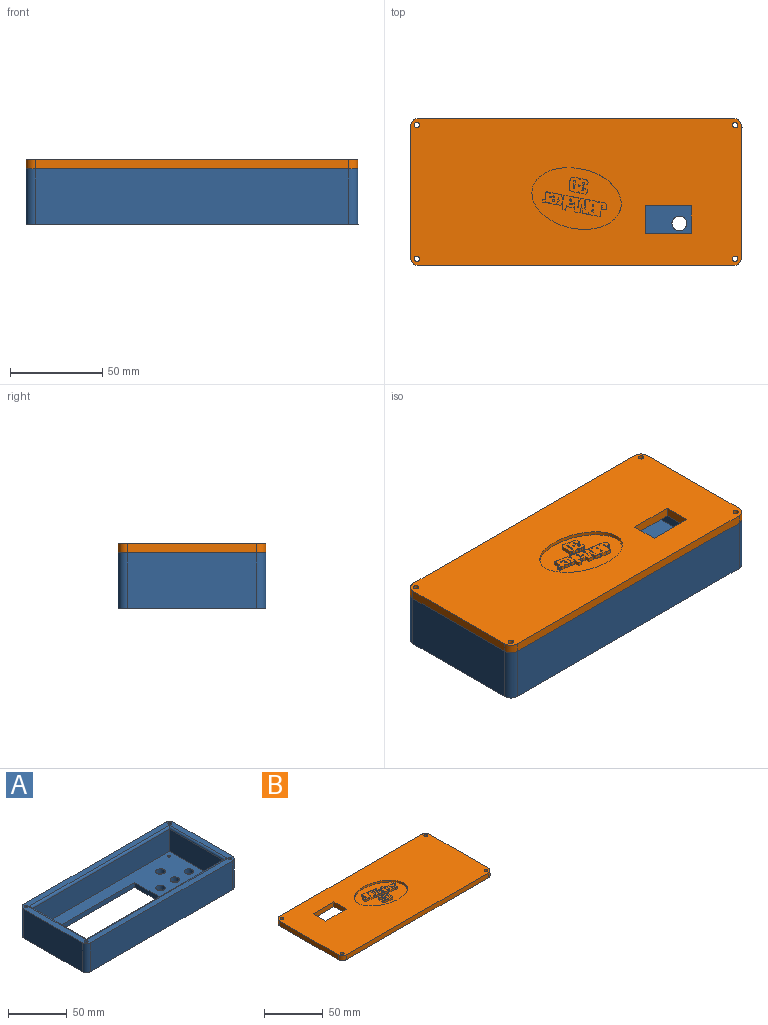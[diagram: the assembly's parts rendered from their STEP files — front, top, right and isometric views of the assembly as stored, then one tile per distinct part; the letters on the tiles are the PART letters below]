
ASSEMBLY  parts=2 mates=1
PART A: 36 faces, bbox 180x80x30 mm
  f0: plane 165x65mm, normal (0,0,1), area 6145.4mm2, adj f2,f3,f4,f9,f11,f12,f13,f14
  f1: plane 180x80mm, normal (0,0,-1), area 9770.7mm2, adj f5,f6,f7,f8,f11,f12,f13,f14
  f2: plane 165x23mm, normal (0,1,0), area 3795mm2, adj f0,f3,f9,f32
  f3: plane 65x23mm, normal (1,0,0), area 1495mm2, adj f0,f2,f4,f33
  f4: plane 165x23mm, normal (0,-1,0), area 3795mm2, adj f0,f3,f9,f35
  f5: plane 70x30mm, normal (-1,0,0), area 2100mm2, adj f1,f10,f28,f31
  f6: plane 170x30mm, normal (0,-1,0), area 5100mm2, adj f1,f10,f28,f29
  f7: plane 70x30mm, normal (1,0,0), area 2100mm2, adj f1,f10,f29,f30
  f8: plane 170x30mm, normal (0,1,0), area 5100mm2, adj f1,f10,f30,f31
  f9: plane 65x23mm, normal (-1,0,0), area 1495mm2, adj f0,f2,f4,f34
  f10: plane 180x80mm, normal (0,0,1), area 2689.3mm2, adj f5,f6,f7,f8,f24,f25,f26,f27
  f11: cylinder r=1.5mm len=5mm, axis (0,0,1), area 47.1mm2, adj f0,f1
  f12: cylinder r=4mm len=8mm, axis (0,0,1), area 125.7mm2, adj f0,f1
  f13: plane 100x5mm, normal (0,-1,0), area 500mm2, adj f0,f1,f14,f16
  f14: plane 43x5mm, normal (1,0,0), area 215mm2, adj f0,f1,f13,f15
  f15: plane 100x5mm, normal (0,1,0), area 500mm2, adj f0,f1,f14,f16
  f16: plane 43x5mm, normal (-1,0,0), area 215mm2, adj f0,f1,f13,f15
  f17: cylinder r=1.5mm len=5mm, axis (0,0,1), area 47.1mm2, adj f0,f1
  f18: cylinder r=1.5mm len=5mm, axis (0,0,1), area 47.1mm2, adj f0,f1
  f19: cylinder r=1.5mm len=5mm, axis (0,0,1), area 47.1mm2, adj f0,f1
  f20: cylinder r=4mm len=8mm, axis (0,0,1), area 125.7mm2, adj f0,f1
  f21: cylinder r=4mm len=8mm, axis (0,0,1), area 125.7mm2, adj f0,f1
  f22: cylinder r=4mm len=8mm, axis (0,0,1), area 125.7mm2, adj f0,f1
  f23: cylinder r=4mm len=8mm, axis (0,0,1), area 125.7mm2, adj f0,f1
  f24: cylinder r=1.5mm len=30mm, axis (0,0,1), area 282.7mm2, adj f1,f10
  f25: cylinder r=1.5mm len=30mm, axis (0,0,1), area 282.7mm2, adj f1,f10
  f26: cylinder r=1.5mm len=30mm, axis (0,0,1), area 282.7mm2, adj f1,f10
  f27: cylinder r=1.5mm len=30mm, axis (0,0,1), area 282.7mm2, adj f1,f10
  f28: cylinder r=5mm len=30mm, axis (0,0,1), area 235.6mm2, adj f1,f5,f6,f10
  f29: cylinder r=5mm len=30mm, axis (0,0,-1), area 235.6mm2, adj f1,f6,f7,f10
  f30: cylinder r=5mm len=30mm, axis (0,0,1), area 235.6mm2, adj f1,f7,f8,f10
  f31: cylinder r=5mm len=30mm, axis (0,0,-1), area 235.6mm2, adj f1,f5,f8,f10
  f32: cylinder r=2mm len=169mm, axis (1,0,0), area 522.9mm2, adj f2,f10,f33,f34
  f33: cylinder r=2mm len=69mm, axis (0,-1,0), area 208.8mm2, adj f3,f10,f32,f35
  f34: cylinder r=2mm len=69mm, axis (0,1,0), area 208.8mm2, adj f9,f10,f32,f35
  f35: cylinder r=2mm len=169mm, axis (-1,0,0), area 522.9mm2, adj f4,f10,f33,f34
PART B: 155 faces, bbox 180x80x5 mm
  f0: plane 180x80mm, normal (0,0,1), area 12718.4mm2, adj f1,f2,f3,f4,f5,f6,f7,f8
  f1: plane 70x5mm, normal (-1,0,0), area 350mm2, adj f0,f9,f151,f154
  f2: plane 170x5mm, normal (0,-1,0), area 850mm2, adj f0,f9,f151,f152
  f3: plane 70x5mm, normal (1,0,0), area 350mm2, adj f0,f9,f152,f153
  f4: cylinder r=1.5mm len=5mm, axis (0,0,-1), area 47.1mm2, adj f0,f9
  f5: cylinder r=1.5mm len=5mm, axis (0,0,-1), area 47.1mm2, adj f0,f9
  f6: cylinder r=1.5mm len=5mm, axis (0,0,-1), area 47.1mm2, adj f0,f9
  f7: cylinder r=1.5mm len=5mm, axis (0,0,-1), area 47.1mm2, adj f0,f9
  f8: plane 170x5mm, normal (0,1,0), area 850mm2, adj f0,f9,f153,f154
  f9: plane 180x80mm, normal (0,0,-1), area 13975.3mm2, adj f1,f2,f3,f4,f5,f6,f7,f8
  f10: plane 15x5mm, normal (1,0,0), area 75mm2, adj f0,f9,f11,f13
  f11: plane 25x5mm, normal (0,-1,0), area 125mm2, adj f0,f9,f10,f12
  f12: plane 15x5mm, normal (-1,0,0), area 75mm2, adj f0,f9,f11,f13
  f13: plane 25x5mm, normal (0,1,0), area 125mm2, adj f0,f9,f10,f12
  f14: extruded ~8.2x5.11mm, area 39.2mm2, adj f15,f98,f99,f112
  f15: plane 2x0.47mm, normal (0.99,-0.11,0), area 0.9mm2, adj f14,f16,f99,f112
  f16: plane 2x0.4mm, normal (-0.6,0.8,0), area 1mm2, adj f15,f17,f99,f112
  f17: plane 2x0.4mm, normal (-0.6,0.8,0), area 1mm2, adj f16,f18,f99,f112
  f18: plane 2x1.54mm, normal (0.18,0.98,0), area 3.1mm2, adj f17,f19,f99,f112
  f19: extruded ~7.31x4.45mm, area 32.1mm2, adj f18,f20,f99,f112
  f20: plane 2x0.26mm, normal (-0.62,0.79,0), area 0.7mm2, adj f19,f21,f99,f112
  f21: plane 2x1.63mm, normal (0.18,0.98,0), area 3.3mm2, adj f20,f22,f99,f112
  f22: extruded ~5.16x2mm, area 12.2mm2, adj f21,f23,f99,f112
  f23: plane 2x0.48mm, normal (0.14,0.99,0), area 1mm2, adj f22,f24,f99,f112
  f24: plane 2x0.69mm, normal (1,-0.06,0), area 1.4mm2, adj f23,f25,f99,f112
  f25: extruded ~4.92x2.84mm, area 15mm2, adj f24,f26,f99,f112
  f26: plane 2x0mm, normal (-0.9,-0.44,0), area 0mm2, adj f25,f27,f99,f112
  f27: extruded ~2x0.93mm, area 2.4mm2, adj f26,f28,f99,f112
  f28: plane 2x0.29mm, normal (-1,-0.09,0), area 0.6mm2, adj f27,f29,f99,f112
  f29: plane 2x0.31mm, normal (0.6,-0.8,0), area 0.8mm2, adj f28,f30,f99,f112
  f30: plane 2x0.31mm, normal (0.6,-0.8,0), area 0.8mm2, adj f29,f31,f99,f112
  f31: plane 2.77x2mm, normal (-0.18,-0.98,0), area 5.6mm2, adj f30,f32,f99,f112
  f32: extruded ~14.2x7.71mm, area 58.3mm2, adj f31,f33,f99,f112
  f33: plane 2x0.9mm, normal (-0.19,-0.98,0), area 1.8mm2, adj f32,f34,f99,f112
  f34: plane 2.05x2mm, normal (-0.99,-0.11,0), area 4.1mm2, adj f33,f35,f99,f112
  f35: extruded ~3x2mm, area 6mm2, adj f34,f36,f99,f112
  f36: plane 2x0.95mm, normal (-1,-0.08,0), area 1.9mm2, adj f35,f37,f99,f112
  f37: plane 2x1.05mm, normal (1,-0.06,0), area 2.1mm2, adj f36,f38,f99,f112
  f38: extruded ~4.72x2mm, area 12mm2, adj f37,f39,f99,f112
  f39: plane 2x0.55mm, normal (-0.19,-0.98,0), area 1.1mm2, adj f38,f40,f99,f112
  f40: plane 2x0.43mm, normal (-0.99,0.14,0), area 0.9mm2, adj f39,f41,f99,f112
  f41: extruded ~2x0.61mm, area 2.1mm2, adj f40,f42,f99,f112
  f42: plane 2x0.37mm, normal (0.6,-0.8,0), area 0.9mm2, adj f41,f43,f99,f112
  f43: plane 2x1.93mm, normal (-0.19,-0.98,0), area 3.9mm2, adj f42,f44,f99,f112
  f44: plane 2x1.93mm, normal (-0.19,-0.98,0), area 3.9mm2, adj f43,f45,f99,f112
  f45: plane 2x0.4mm, normal (-1,0.06,0), area 0.8mm2, adj f44,f46,f99,f112
  f46: extruded ~2x0.56mm, area 2mm2, adj f45,f47,f99,f112
  f47: plane 2x0.36mm, normal (0.57,-0.82,0), area 0.9mm2, adj f46,f48,f99,f112
  f48: plane 2x1.42mm, normal (-0.18,-0.98,0), area 2.9mm2, adj f47,f49,f99,f112
  f49: plane 2x1.42mm, normal (-0.18,-0.98,0), area 2.9mm2, adj f48,f50,f99,f112
  f50: plane 2x0.46mm, normal (-0.77,-0.63,0), area 1.2mm2, adj f49,f51,f99,f112
  f51: extruded ~2.02x2mm, area 4.4mm2, adj f50,f52,f99,f112
  f52: plane 2x1.18mm, normal (-1,0.08,0), area 2.4mm2, adj f51,f53,f99,f112
  f53: plane 2x0.7mm, normal (0.09,1,0), area 1.4mm2, adj f52,f54,f99,f112
  f54: extruded ~2x1.04mm, area 2.1mm2, adj f53,f55,f99,f112
  f55: plane 2x0.34mm, normal (0,1,0), area 0.7mm2, adj f54,f56,f99,f112
  f56: plane 2x0.99mm, normal (1,-0.06,0), area 2mm2, adj f55,f57,f99,f112
  f57: plane 2x0.99mm, normal (1,-0.06,0), area 2mm2, adj f56,f58,f99,f112
  f58: plane 2x0.36mm, normal (0.17,0.98,0), area 0.7mm2, adj f57,f59,f99,f112
  f59: extruded ~6.06x3.81mm, area 18.9mm2, adj f58,f60,f99,f112
  f60: plane 2.88x2mm, normal (0.19,0.98,0), area 5.9mm2, adj f59,f98,f99,f112
  f61: plane 2x0.97mm, normal (-0.32,-0.95,0), area 2.1mm2, adj f62,f96,f99,f100
  f62: plane 2x0.3mm, normal (-1,0,0), area 0.6mm2, adj f61,f63,f99,f100
  f63: extruded ~2x1.71mm, area 4mm2, adj f62,f64,f99,f100
  f64: plane 2x0.58mm, normal (-0.59,0.81,0), area 1.4mm2, adj f63,f65,f99,f100
  f65: plane 2x1.41mm, normal (0.18,0.98,0), area 2.9mm2, adj f64,f66,f99,f100
  f66: plane 2x1.41mm, normal (0.18,0.98,0), area 2.9mm2, adj f65,f67,f99,f100
  f67: plane 2x0.37mm, normal (0.8,0.6,0), area 0.9mm2, adj f66,f68,f99,f100
  f68: extruded ~2.66x2mm, area 7mm2, adj f67,f69,f99,f100
  f69: plane 2x1.78mm, normal (0.18,0.98,0), area 3.6mm2, adj f68,f70,f99,f100
  f70: plane 2x0.45mm, normal (0.77,0.64,0), area 1.2mm2, adj f69,f71,f99,f100
  f71: extruded ~7.44x3.58mm, area 20.5mm2, adj f70,f72,f99,f100
  f72: plane 2x1.78mm, normal (-0.19,-0.98,0), area 3.6mm2, adj f71,f73,f99,f100
  f73: plane 2x0.36mm, normal (-1,-0.08,0), area 0.7mm2, adj f72,f74,f99,f100
  f74: extruded ~2x0.48mm, area 1.7mm2, adj f73,f75,f99,f100
  f75: plane 2x0.37mm, normal (0.6,-0.8,0), area 0.9mm2, adj f74,f76,f99,f100
  f76: plane 2x1.46mm, normal (-0.19,-0.98,0), area 3mm2, adj f75,f77,f99,f100
  f77: extruded ~2.38x2.33mm, area 7.6mm2, adj f76,f78,f99,f100
  f78: plane 2x0.83mm, normal (-1,0.07,0), area 1.7mm2, adj f77,f79,f99,f100
  f79: plane 2x0.7mm, normal (0.09,1,0), area 1.4mm2, adj f78,f80,f99,f100
  f80: extruded ~2x1.05mm, area 2.1mm2, adj f79,f81,f99,f100
  f81: plane 2x0.35mm, normal (0,1,0), area 0.7mm2, adj f80,f82,f99,f100
  f82: plane 2x1.31mm, normal (1,-0.04,0), area 2.6mm2, adj f81,f83,f99,f100
  f83: plane 2x0.37mm, normal (0.15,0.99,0), area 0.8mm2, adj f82,f84,f99,f100
  f84: extruded ~2x0.8mm, area 2.4mm2, adj f83,f85,f99,f100
  f85: plane 2x0.76mm, normal (-1,0.07,0), area 1.5mm2, adj f84,f86,f99,f100
  f86: plane 2x0.41mm, normal (-0.16,-0.99,0), area 0.8mm2, adj f85,f87,f99,f100
  f87: extruded ~2x1.07mm, area 2.7mm2, adj f86,f88,f99,f100
  f88: plane 2x0.42mm, normal (-1,0,0), area 0.8mm2, adj f87,f89,f99,f100
  f89: plane 2x0.42mm, normal (0.14,0.99,0), area 0.9mm2, adj f88,f90,f99,f100
  f90: plane 2x0.42mm, normal (0.14,0.99,0), area 0.9mm2, adj f89,f91,f99,f100
  f91: plane 2x0.69mm, normal (-1,0.08,0), area 1.4mm2, adj f90,f92,f99,f100
  f92: extruded ~2x0.82mm, area 2.3mm2, adj f91,f93,f99,f100
  f93: plane 2x0.41mm, normal (-0.15,-0.99,0), area 0.8mm2, adj f92,f94,f99,f100
  f94: plane 2x0.53mm, normal (1,0,0), area 1.1mm2, adj f93,f96,f99,f100
  f95: extruded ~48.38x33.43mm, area 259.3mm2, adj f0,f97,f99
  f96: extruded ~2x1.11mm, area 3.4mm2, adj f61,f94,f99,f100
  f97: plane 2x0mm, normal (-1,0,0), area 0mm2, adj f0,f95,f99
  f98: plane 2x0.34mm, normal (0.78,0.63,0), area 0.9mm2, adj f14,f60,f99,f112
  f99: plane 48.73x33.69mm, normal (0,0,1), area 946.9mm2, adj f14,f15,f16,f17,f18,f19,f20,f21
  f100: plane 10.09x9.31mm, normal (0,0,1), area 63.6mm2, adj f61,f62,f63,f64,f65,f66,f67,f68
  f101: plane 2x0.57mm, normal (-0.99,0.11,0), area 1.1mm2, adj f100,f102,f106,f107
  f102: extruded ~2x0.63mm, area 1.3mm2, adj f100,f101,f103,f107
  f103: extruded ~2x0.34mm, area 0.8mm2, adj f100,f102,f104,f107
  f104: plane 2x0.32mm, normal (0.63,-0.77,0), area 0.8mm2, adj f100,f103,f105,f107
  f105: plane 2x0.37mm, normal (0.8,0.6,0), area 0.9mm2, adj f100,f104,f106,f107
  f106: plane 2x0.37mm, normal (0.8,0.6,0), area 0.9mm2, adj f100,f101,f105,f107
  f107: plane 1.2x0.67mm, normal (0,0,1), area 0.4mm2, adj f101,f102,f103,f104,f105,f106
  f108: plane 2x1.86mm, normal (-1,0.08,0), area 3.7mm2, adj f100,f109,f110,f111
  f109: extruded ~4.43x2mm, area 15.8mm2, adj f100,f108,f110,f111
  f110: plane 2x0.26mm, normal (-0.07,1,0), area 0.5mm2, adj f100,f108,f109,f111
  f111: plane 4.47x1.12mm, normal (0,0,1), area 3.4mm2, adj f108,f109,f110
  f112: plane 34.66x13.59mm, normal (0,0,1), area 223mm2, adj f14,f15,f16,f17,f18,f19,f20,f21
  f113: cylinder r=0.65mm len=2mm, axis (0,0,1), area 1.6mm2, adj f112,f114,f118,f119
  f114: extruded ~2x0.36mm, area 0.7mm2, adj f112,f113,f115,f119
  f115: plane 2x0mm, normal (0.41,-0.91,0), area 0mm2, adj f112,f114,f116,f119
  f116: extruded ~2x0.67mm, area 2.1mm2, adj f112,f115,f117,f119
  f117: plane 2x0.3mm, normal (-0.08,-1,0), area 0.6mm2, adj f112,f116,f118,f119
  f118: plane 2x1.17mm, normal (1,0,0), area 2.3mm2, adj f112,f113,f117,f119
  f119: plane 1.23x0.82mm, normal (0,0,1), area 0.9mm2, adj f113,f114,f115,f116,f117,f118
  f120: cylinder r=0.68mm len=2mm, axis (0,0,1), area 4.3mm2, adj f112,f121,f125,f126
  f121: extruded ~2x0.24mm, area 0.5mm2, adj f112,f120,f122,f126
  f122: cylinder r=0.68mm len=2mm, axis (0,0,1), area 0.4mm2, adj f112,f121,f123,f126
  f123: plane 2x0.07mm, normal (1,-0.01,0), area 0.1mm2, adj f112,f122,f124,f126
  f124: extruded ~2x0.06mm, area 0.1mm2, adj f112,f123,f125,f126
  f125: plane 2x1.18mm, normal (1,-0.01,0), area 2.4mm2, adj f112,f120,f124,f126
  f126: plane 1.37x0.91mm, normal (0,0,1), area 1mm2, adj f120,f121,f122,f123,f124,f125
  f127: plane 2x0mm, normal (0.98,0.2,0), area 0mm2, adj f112,f128,f129
  f128: extruded ~2.71x2mm, area 13.9mm2, adj f112,f127,f129
  f129: plane 2.74x0.87mm, normal (0,0,1), area 1.2mm2, adj f127,f128
  f130: plane 2x0mm, normal (0,1,0), area 0mm2, adj f112,f131,f132
  f131: extruded ~2x1.19mm, area 7.2mm2, adj f112,f130,f132
  f132: plane 1.21x0.99mm, normal (0,0,1), area 1mm2, adj f130,f131
  f133: plane 2x1.31mm, normal (-0.05,-1,0), area 2.6mm2, adj f112,f134,f136,f137
  f134: extruded ~2x1.46mm, area 5.9mm2, adj f112,f133,f135,f137
  f135: extruded ~2x1.91mm, area 4.6mm2, adj f112,f134,f136,f137
  f136: plane 2x0.32mm, normal (-1,0,0), area 0.6mm2, adj f112,f133,f135,f137
  f137: plane 2.8x0.84mm, normal (0,0,1), area 1.7mm2, adj f133,f134,f135,f136
  f138: extruded ~2x0.91mm, area 3.3mm2, adj f112,f139,f142,f143
  f139: plane 2x0mm, normal (0.11,-0.99,0), area 0mm2, adj f112,f138,f140,f143
  f140: extruded ~2x0.57mm, area 2mm2, adj f112,f139,f141,f143
  f141: plane 2x0.45mm, normal (-0.13,-0.99,0), area 0.9mm2, adj f112,f140,f142,f143
  f142: plane 2x0.48mm, normal (1,0,0), area 1mm2, adj f112,f138,f141,f143
  f143: plane 1.07x0.96mm, normal (0,0,1), area 0.9mm2, adj f138,f139,f140,f141,f142
  f144: plane 2x0.62mm, normal (-1,0.09,0), area 1.2mm2, adj f112,f145,f149,f150
  f145: extruded ~2x1.48mm, area 3mm2, adj f112,f144,f146,f150
  f146: plane 2x0.86mm, normal (-1,0.07,0), area 1.7mm2, adj f112,f145,f147,f150
  f147: plane 2x1.28mm, normal (0.85,-0.53,0), area 3mm2, adj f112,f146,f148,f150
  f148: plane 2x0.84mm, normal (0.95,0.32,0), area 1.8mm2, adj f112,f147,f149,f150
  f149: plane 2x0.84mm, normal (0.95,0.32,0), area 1.8mm2, adj f112,f144,f148,f150
  f150: plane 2.95x0.79mm, normal (0,0,1), area 1mm2, adj f144,f145,f146,f147,f148,f149
  f151: cylinder r=5mm len=5mm, axis (0,0,1), area 39.3mm2, adj f0,f1,f2,f9
  f152: cylinder r=5mm len=5mm, axis (0,0,-1), area 39.3mm2, adj f0,f2,f3,f9
  f153: cylinder r=5mm len=5mm, axis (0,0,1), area 39.3mm2, adj f0,f3,f8,f9
  f154: cylinder r=5mm len=5mm, axis (0,0,-1), area 39.3mm2, adj f0,f1,f8,f9
PLACE A t=(-190.93,7.24,-45.06)mm
PLACE B rot(axis=(0,0,1),180deg) t=(-471.66,15.48,-15.06)mm
MATE fastened B.f5 <-> A.f25  axis (0,0,-1) through (-277.18,-29.01,-15.06)mm
